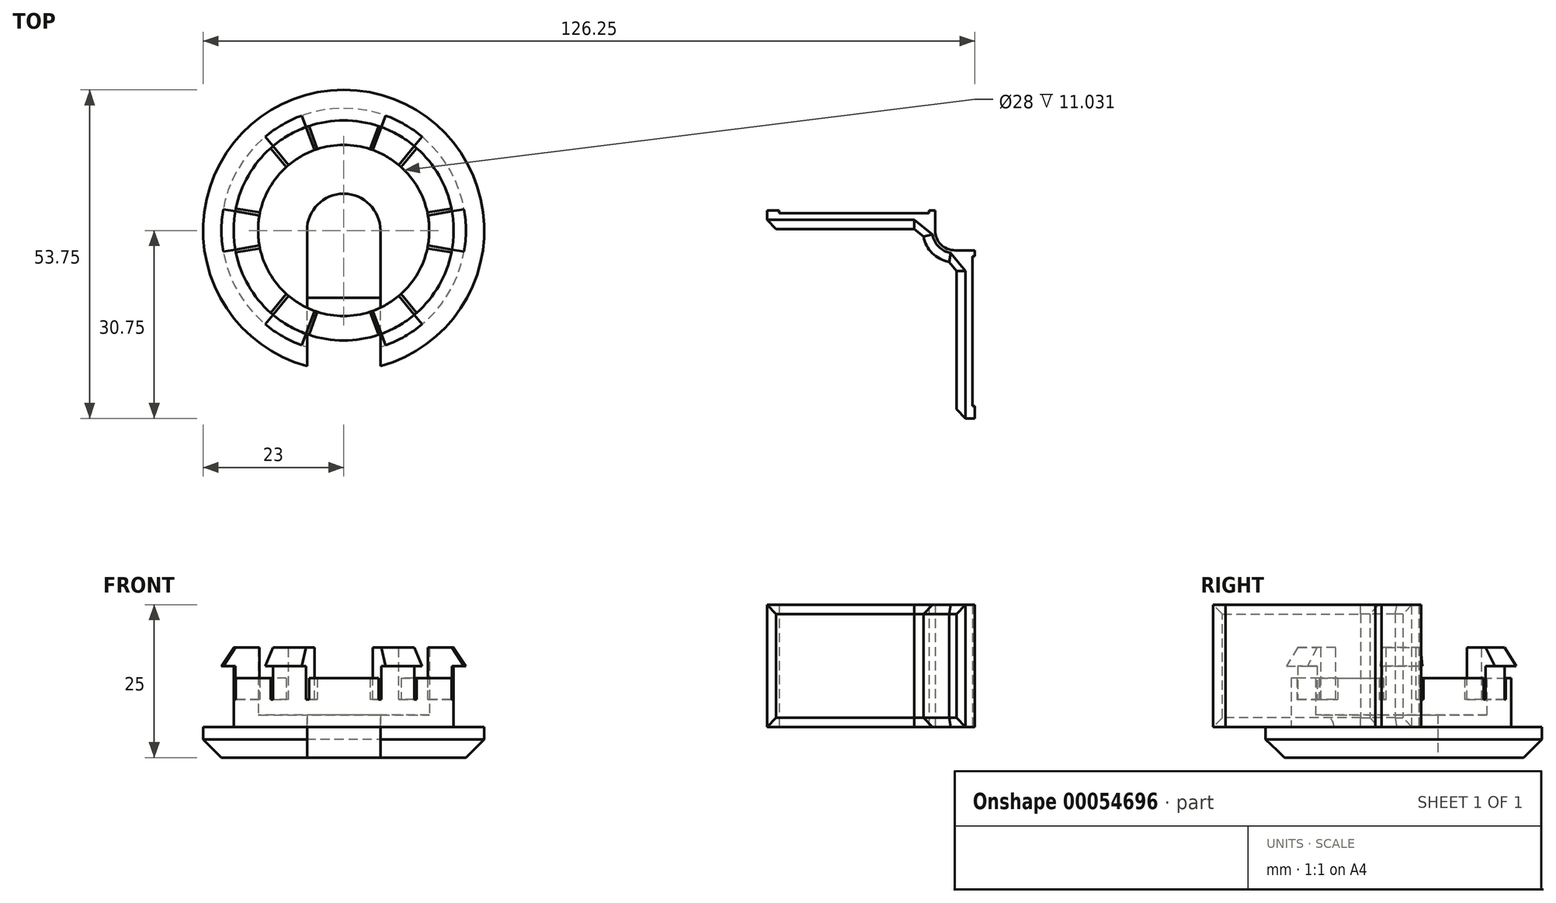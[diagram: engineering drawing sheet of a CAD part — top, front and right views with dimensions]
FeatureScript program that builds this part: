
annotation { "Feature Type Name" : "Feature", "Feature Type Description" : "" }
export const myFeature = defineFeature(function(context is Context, id is Id, definition is map)
    precondition{}
    {
        {
            var Q0;
            Q0=qCreatedBy(makeId("Top.planeOp"),FACE);
            var sketch = newSketch(context, id + "F0", { "sketchPlane" : qUnion([Q0])});
            skCircle(sketch, "E0", {"center": v(0, 0) * mm, "radius": 18 * mm});
            skCircle(sketch, "E1", {"center": v(0, 0) * mm, "radius": 6 * mm});
            skCircle(sketch, "E2", {"center": v(0, 0) * mm, "radius": 23 * mm});
            skCircle(sketch, "E3", {"center": v(0, 0) * mm, "radius": 14 * mm});
            skSolve(sketch);
        }
        {
            var Q0;
            Q0=makeQuery(id+"F0.imprint","IMPRINT",FACE,{"disambiguationData":[TD([[makeQuery(id+"F0.imprint","IMPRINT",EDGE,{"derivedFrom":sQuery(id+"F0.wireOp",EDGE,"E0")}),1.0]])]});
            var Q1;
            Q1=makeQuery(id+"F0.imprint","IMPRINT",FACE,{"disambiguationData":[TD([[makeQuery(id+"F0.imprint","IMPRINT",EDGE,{"derivedFrom":sQuery(id+"F0.wireOp",EDGE,"E1")}),-1.0]])]});
            extrude(context, id + "F1", {"entities" : qUnion([Q0, Q1]), "depth" : 2 * mm});
        }
        {
            var Q0;
            Q0=makeQuery(id+"F0.imprint","IMPRINT",FACE,{"disambiguationData":[TD([[makeQuery(id+"F0.imprint","IMPRINT",EDGE,{"derivedFrom":sQuery(id+"F0.wireOp",EDGE,"E0")}),1.0]])]});
            extrude(context, id + "F2", {"entities" : qUnion([Q0]), "operationType" : NewBodyOperationType.ADD, "depth" : 13 * mm});
        }
        {
            var Q0;
            Q0=makeQuery(id+"F0.imprint","IMPRINT",FACE,{"disambiguationData":[TD([[makeQuery(id+"F0.imprint","IMPRINT",EDGE,{"derivedFrom":sQuery(id+"F0.wireOp",EDGE,"E0")}),-1.0]])]});
            var Q1;
            Q1=makeQuery(id+"F0.imprint","IMPRINT",FACE,{"disambiguationData":[TD([[makeQuery(id+"F0.imprint","IMPRINT",EDGE,{"derivedFrom":sQuery(id+"F0.wireOp",EDGE,"E0")}),1.0]])]});
            var Q2;
            Q2=makeQuery(id+"F0.imprint","IMPRINT",FACE,{"disambiguationData":[TD([[makeQuery(id+"F0.imprint","IMPRINT",EDGE,{"derivedFrom":sQuery(id+"F0.wireOp",EDGE,"E1")}),-1.0]])]});
            extrude(context, id + "F3", {"entities" : qUnion([Q0, Q1, Q2]), "operationType" : NewBodyOperationType.ADD, "oppositeDirection" : true, "depth" : 5 * mm});
        }
        {
            var Q0;
            Q0=makeQuery(id+"F3.opExtrude","CAP_EDGE",EDGE,{"disambiguationData":[OSD([sQuery(id+"F0.wireOp",EDGE,"E2")])],"isStart":false});
            chamfer(context, id + "F4", {"entities" : qUnion([Q0]), "width" : 3 * mm, "tangentPropagation" : true});
        }
        {
            var Q0;
            Q0=qCreatedBy(makeId("Right.planeOp"),FACE);
            var sketch = newSketch(context, id + "F5", { "sketchPlane" : qUnion([Q0])});
            skLineSegment(sketch, "E4", {"start": v(0, 30.83) * mm, "end": v(0, -5) * mm});
            skLineSegment(sketch, "E5", {"start": v(0, -5) * mm, "end": v(-46.75, -5) * mm});
            skLineSegment(sketch, "E6", {"start": v(-46.75, -5) * mm, "end": v(-46.75, 0) * mm});
            skLineSegment(sketch, "E7", {"start": v(-46.75, 0) * mm, "end": v(-11, 0) * mm});
            skLineSegment(sketch, "E8", {"start": v(-11, 0) * mm, "end": v(-6, 5) * mm});
            skLineSegment(sketch, "E9", {"start": v(-6, 5) * mm, "end": v(-6, 30.83) * mm});
            skLineSegment(sketch, "E10", {"start": v(-6, 30.83) * mm, "end": v(0, 30.83) * mm});
            skSolve(sketch);
        }
        {
            var Q0;
            Q0=makeQuery(id+"F5.imprint","IMPRINT",FACE,{"disambiguationData":[TD([[makeQuery(id+"F5.imprint","IMPRINT",EDGE,{"derivedFrom":sQuery(id+"F5.wireOp",EDGE,"E4")}),-1.0]])]});
            extrude(context, id + "F6", {"entities" : qUnion([Q0]), "operationType" : NewBodyOperationType.REMOVE, "endBound" : BoundingType.SYMMETRIC, "oppositeDirection" : true, "depth" : 12 * mm});
        }
        {
            var Q0;
            Q0=makeQuery(id+"F6.boolean.opBoolean","INTERSECT",EDGE,{"derivedFrom":[makeQuery(id+"F1.opExtrude","CAP_FACE",FACE,{"disambiguationData":[OSD([sQuery(id+"F0.wireOp",EDGE,"E0"),sQuery(id+"F0.wireOp",EDGE,"E1")])],"isStart":false}),makeQuery(id+"F6.opExtrude","SWEPT_FACE",FACE,{"disambiguationData":[OSD([sQuery(id+"F5.wireOp",EDGE,"E8")])]})]});
            fillet(context, id + "F7", {"entities" : qUnion([Q0]), "radius" : 2 * mm, "tangentPropagation" : true, "allowEdgeOverflow" : false});
        }
        {
            var Q0;
            Q0=qCreatedBy(makeId("Front.planeOp"),FACE);
            var sketch = newSketch(context, id + "F8", { "sketchPlane" : qUnion([Q0])});
            skLineSegment(sketch, "E11", {"start": v(14, 10) * mm, "end": v(14, 13) * mm});
            skLineSegment(sketch, "E12", {"start": v(14, 13) * mm, "end": v(18, 13) * mm});
            skLineSegment(sketch, "E13", {"start": v(18, 13) * mm, "end": v(20, 10) * mm});
            skLineSegment(sketch, "E14", {"start": v(20, 10) * mm, "end": v(14, 10) * mm});
            skLineSegment(sketch, "E15", {"start": v(0, 0) * mm, "end": v(0, 19.84) * mm});
            skLineSegment(sketch, "E16", {"start": v(18, 13) * mm, "end": v(18, 5) * mm});
            skLineSegment(sketch, "E17", {"start": v(18, 5) * mm, "end": v(14, 5) * mm});
            skLineSegment(sketch, "E18", {"start": v(14, 5) * mm, "end": v(14, 10) * mm});
            skSolve(sketch);
        }
        {
            var Q0;
            Q0=makeQuery(id+"F8.imprint","IMPRINT",FACE,{"disambiguationData":[TD([[makeQuery(id+"F8.imprint","IMPRINT",EDGE,{"derivedFrom":sQuery(id+"F8.wireOp",EDGE,"E11")}),-1.0]])]});
            var Q1;
            {var subQ0=sQuery(id+"F8.wireOp",EDGE,"E13");Q1=makeQuery(id+"F8.imprint","IMPRINT",FACE,{"disambiguationData":[TD([[makeQuery(id+"F8.imprint","IMPRINT",EDGE,{"derivedFrom":subQ0}),-1.0]])]});}
            var Q2;
            {var subQ4=sQuery(id+"F8.wireOp",EDGE,"E17");Q2=makeQuery(id+"F8.imprint","IMPRINT",FACE,{"disambiguationData":[TD([[makeQuery(id+"F8.imprint","IMPRINT",EDGE,{"derivedFrom":subQ4}),-1.0]])]});}
            var Q3;
            Q3=sQuery(id+"F8.wireOp",EDGE,"E15");
            revolve(context, id + "F9", {"entities" : qUnion([Q0, Q1, Q2]), "axis" : qUnion([Q3]), "revolveType" : RevolveType.SYMMETRIC, "angle" : 20 * degree});
        }
        {
            var Q0;
            Q0=makeQuery(id+"F9.opRevolve","SWEPT_BODY",BODY,{"disambiguationData":[OSD([sQuery(id+"F8.wireOp",EDGE,"E11"),sQuery(id+"F8.wireOp",EDGE,"E12"),sQuery(id+"F8.wireOp",EDGE,"E13"),sQuery(id+"F8.wireOp",EDGE,"E14")])]});
            var Q1;
            Q1=sQuery(id+"F8.wireOp",EDGE,"E15");
            circularPattern(context, id + "F10", {"entities" : qUnion([Q0]), "axis" : qUnion([Q1]), "angle" : 360 * degree, "instanceCount" : 6, "equalSpace" : true});
        }
        {
            var Q0;
            Q0=makeQuery(id+"F9.opRevolve","SWEPT_BODY",BODY,{"disambiguationData":[OSD([sQuery(id+"F8.wireOp",EDGE,"E11"),sQuery(id+"F8.wireOp",EDGE,"E12"),sQuery(id+"F8.wireOp",EDGE,"E13"),sQuery(id+"F8.wireOp",EDGE,"E14"),sQuery(id+"F8.wireOp",EDGE,"E16"),sQuery(id+"F8.wireOp",EDGE,"E17"),sQuery(id+"F8.wireOp",EDGE,"E18")])]});
            var Q1;
            Q1=makeQuery(id+"F10.opPattern","COPY",BODY,{"derivedFrom":makeQuery(id+"F9.opRevolve","SWEPT_BODY",BODY,{"disambiguationData":[OSD([sQuery(id+"F8.wireOp",EDGE,"E11"),sQuery(id+"F8.wireOp",EDGE,"E12"),sQuery(id+"F8.wireOp",EDGE,"E13"),sQuery(id+"F8.wireOp",EDGE,"E14"),sQuery(id+"F8.wireOp",EDGE,"E16"),sQuery(id+"F8.wireOp",EDGE,"E17"),sQuery(id+"F8.wireOp",EDGE,"E18")])]}),"instanceName":"1"});
            var Q2;
            Q2=makeQuery(id+"F10.opPattern","COPY",BODY,{"derivedFrom":makeQuery(id+"F9.opRevolve","SWEPT_BODY",BODY,{"disambiguationData":[OSD([sQuery(id+"F8.wireOp",EDGE,"E11"),sQuery(id+"F8.wireOp",EDGE,"E12"),sQuery(id+"F8.wireOp",EDGE,"E13"),sQuery(id+"F8.wireOp",EDGE,"E14"),sQuery(id+"F8.wireOp",EDGE,"E16"),sQuery(id+"F8.wireOp",EDGE,"E17"),sQuery(id+"F8.wireOp",EDGE,"E18")])]}),"instanceName":"2"});
            var Q3;
            Q3=makeQuery(id+"F10.opPattern","COPY",BODY,{"derivedFrom":makeQuery(id+"F9.opRevolve","SWEPT_BODY",BODY,{"disambiguationData":[OSD([sQuery(id+"F8.wireOp",EDGE,"E11"),sQuery(id+"F8.wireOp",EDGE,"E12"),sQuery(id+"F8.wireOp",EDGE,"E13"),sQuery(id+"F8.wireOp",EDGE,"E14"),sQuery(id+"F8.wireOp",EDGE,"E16"),sQuery(id+"F8.wireOp",EDGE,"E17"),sQuery(id+"F8.wireOp",EDGE,"E18")])]}),"instanceName":"3"});
            var Q4;
            Q4=makeQuery(id+"F10.opPattern","COPY",BODY,{"derivedFrom":makeQuery(id+"F9.opRevolve","SWEPT_BODY",BODY,{"disambiguationData":[OSD([sQuery(id+"F8.wireOp",EDGE,"E11"),sQuery(id+"F8.wireOp",EDGE,"E12"),sQuery(id+"F8.wireOp",EDGE,"E13"),sQuery(id+"F8.wireOp",EDGE,"E14"),sQuery(id+"F8.wireOp",EDGE,"E16"),sQuery(id+"F8.wireOp",EDGE,"E17"),sQuery(id+"F8.wireOp",EDGE,"E18")])]}),"instanceName":"4"});
            var Q5;
            Q5=makeQuery(id+"F10.opPattern","COPY",BODY,{"derivedFrom":makeQuery(id+"F9.opRevolve","SWEPT_BODY",BODY,{"disambiguationData":[OSD([sQuery(id+"F8.wireOp",EDGE,"E11"),sQuery(id+"F8.wireOp",EDGE,"E12"),sQuery(id+"F8.wireOp",EDGE,"E13"),sQuery(id+"F8.wireOp",EDGE,"E14"),sQuery(id+"F8.wireOp",EDGE,"E16"),sQuery(id+"F8.wireOp",EDGE,"E17"),sQuery(id+"F8.wireOp",EDGE,"E18")])]}),"instanceName":"5"});
            var Q6;
            Q6=makeQuery(id+"F1.opExtrude","SWEPT_BODY",BODY,{"disambiguationData":[OSD([sQuery(id+"F0.wireOp",EDGE,"E0"),sQuery(id+"F0.wireOp",EDGE,"E1")])]});
            booleanBodies(context, id + "F11", {"operationType" : BooleanOperationType.SUBTRACTION, "tools" : qUnion([Q0, Q1, Q2, Q3, Q4, Q5]), "targets" : qUnion([Q6]), "offset" : true, "offsetAll" : true, "offsetDistance" : 0.5 * mm, "keepTools" : true});
        }
        {
            var Q0;
            Q0=makeQuery(id+"F10.opPattern","COPY",FACE,{"derivedFrom":makeQuery(id+"F9.opRevolve","SWEPT_FACE",FACE,{"disambiguationData":[OSD([sQuery(id+"F8.wireOp",EDGE,"E17")])]}),"instanceName":"4"});
            var Q1;
            Q1=makeQuery(id+"F10.opPattern","COPY",FACE,{"derivedFrom":makeQuery(id+"F9.opRevolve","SWEPT_FACE",FACE,{"disambiguationData":[OSD([sQuery(id+"F8.wireOp",EDGE,"E17")])]}),"instanceName":"5"});
            var Q2;
            Q2=makeQuery(id+"F9.opRevolve","SWEPT_FACE",FACE,{"disambiguationData":[OSD([sQuery(id+"F8.wireOp",EDGE,"E17")])]});
            var Q3;
            Q3=makeQuery(id+"F10.opPattern","COPY",FACE,{"derivedFrom":makeQuery(id+"F9.opRevolve","SWEPT_FACE",FACE,{"disambiguationData":[OSD([sQuery(id+"F8.wireOp",EDGE,"E17")])]}),"instanceName":"1"});
            var Q4;
            Q4=makeQuery(id+"F10.opPattern","COPY",FACE,{"derivedFrom":makeQuery(id+"F9.opRevolve","SWEPT_FACE",FACE,{"disambiguationData":[OSD([sQuery(id+"F8.wireOp",EDGE,"E17")])]}),"instanceName":"2"});
            var Q5;
            Q5=makeQuery(id+"F10.opPattern","COPY",FACE,{"derivedFrom":makeQuery(id+"F9.opRevolve","SWEPT_FACE",FACE,{"disambiguationData":[OSD([sQuery(id+"F8.wireOp",EDGE,"E17")])]}),"instanceName":"3"});
            extrude(context, id + "F12", {"entities" : qUnion([Q0, Q1, Q2, Q3, Q4, Q5]), "operationType" : NewBodyOperationType.ADD, "depth" : 5 * mm});
        }
        {
            var Q0;
            {var subQ0=sQuery(id+"F8.wireOp",EDGE,"E18");var subQ1=sQuery(id+"F8.wireOp",EDGE,"E17");var subQ2=sQuery(id+"F8.wireOp",EDGE,"E16");var subQ3=sQuery(id+"F8.wireOp",EDGE,"E14");var subQ4=sQuery(id+"F8.wireOp",EDGE,"E13");var subQ5=sQuery(id+"F8.wireOp",EDGE,"E12");var subQ6=sQuery(id+"F8.wireOp",EDGE,"E11");var subQ7=sQuery(id+"F0.wireOp",EDGE,"E0");var subQ8=sQuery(id+"F0.wireOp",EDGE,"E3");Q0=makeQuery(id+"F11.tempBoolean.opBoolean","SPLIT",FACE,{"disambiguationData":[TD([makeQuery(id+"F11.offsetTempBody.opPattern","COPY",FACE,{"derivedFrom":makeQuery(id+"F10.opPattern","COPY",FACE,{"derivedFrom":makeQuery(id+"F9.opRevolve","CAP_FACE",FACE,{"disambiguationData":[OSD([subQ6,subQ5,subQ4,subQ3,subQ2,subQ1,subQ0])],"isStart":false}),"instanceName":"2"}),"instanceName":"1"})])],"derivedFrom":makeQuery(id+"F2.opExtrude","CAP_FACE",FACE,{"disambiguationData":[OSD([subQ7,subQ8])],"isStart":false})});}
            var Q1;
            {var subQ0=sQuery(id+"F0.wireOp",EDGE,"E3");var subQ1=sQuery(id+"F0.wireOp",EDGE,"E0");var subQ2=sQuery(id+"F8.wireOp",EDGE,"E18");var subQ3=sQuery(id+"F8.wireOp",EDGE,"E17");var subQ4=sQuery(id+"F8.wireOp",EDGE,"E16");var subQ5=sQuery(id+"F8.wireOp",EDGE,"E14");var subQ6=sQuery(id+"F8.wireOp",EDGE,"E13");var subQ7=sQuery(id+"F8.wireOp",EDGE,"E12");var subQ8=sQuery(id+"F8.wireOp",EDGE,"E11");Q1=makeQuery(id+"F11.tempBoolean.opBoolean","SPLIT",FACE,{"disambiguationData":[TD([makeQuery(id+"F11.offsetTempBody.opPattern","COPY",FACE,{"derivedFrom":makeQuery(id+"F10.opPattern","COPY",FACE,{"derivedFrom":makeQuery(id+"F9.opRevolve","CAP_FACE",FACE,{"disambiguationData":[OSD([subQ8,subQ7,subQ6,subQ5,subQ4,subQ3,subQ2])],"isStart":false}),"instanceName":"3"}),"instanceName":"1"})])],"derivedFrom":makeQuery(id+"F2.opExtrude","CAP_FACE",FACE,{"disambiguationData":[OSD([subQ1,subQ0])],"isStart":false})});}
            var Q2;
            {var subQ0=sQuery(id+"F8.wireOp",EDGE,"E18");var subQ1=sQuery(id+"F8.wireOp",EDGE,"E17");var subQ2=sQuery(id+"F8.wireOp",EDGE,"E16");var subQ3=sQuery(id+"F8.wireOp",EDGE,"E14");var subQ4=sQuery(id+"F8.wireOp",EDGE,"E13");var subQ5=sQuery(id+"F8.wireOp",EDGE,"E12");var subQ6=sQuery(id+"F8.wireOp",EDGE,"E11");var subQ7=sQuery(id+"F0.wireOp",EDGE,"E3");var subQ8=sQuery(id+"F0.wireOp",EDGE,"E0");Q2=makeQuery(id+"F11.tempBoolean.opBoolean","SPLIT",FACE,{"disambiguationData":[TD([makeQuery(id+"F11.offsetTempBody.opPattern","COPY",FACE,{"derivedFrom":makeQuery(id+"F10.opPattern","COPY",FACE,{"derivedFrom":makeQuery(id+"F9.opRevolve","CAP_FACE",FACE,{"disambiguationData":[OSD([subQ6,subQ5,subQ4,subQ3,subQ2,subQ1,subQ0])],"isStart":false}),"instanceName":"4"}),"instanceName":"1"})])],"derivedFrom":makeQuery(id+"F2.opExtrude","CAP_FACE",FACE,{"disambiguationData":[OSD([subQ8,subQ7])],"isStart":false})});}
            var Q3;
            {var subQ0=sQuery(id+"F0.wireOp",EDGE,"E3");var subQ1=sQuery(id+"F0.wireOp",EDGE,"E0");var subQ2=sQuery(id+"F8.wireOp",EDGE,"E18");var subQ3=sQuery(id+"F8.wireOp",EDGE,"E17");var subQ4=sQuery(id+"F8.wireOp",EDGE,"E16");var subQ5=sQuery(id+"F8.wireOp",EDGE,"E14");var subQ6=sQuery(id+"F8.wireOp",EDGE,"E13");var subQ7=sQuery(id+"F8.wireOp",EDGE,"E12");var subQ8=sQuery(id+"F8.wireOp",EDGE,"E11");Q3=makeQuery(id+"F11.tempBoolean.opBoolean","SPLIT",FACE,{"disambiguationData":[TD([makeQuery(id+"F11.offsetTempBody.opPattern","COPY",FACE,{"derivedFrom":makeQuery(id+"F9.opRevolve","CAP_FACE",FACE,{"disambiguationData":[OSD([subQ8,subQ7,subQ6,subQ5,subQ4,subQ3,subQ2])],"isStart":true}),"instanceName":"1"})])],"derivedFrom":makeQuery(id+"F2.opExtrude","CAP_FACE",FACE,{"disambiguationData":[OSD([subQ1,subQ0])],"isStart":false})});}
            var Q4;
            {var subQ0=sQuery(id+"F0.wireOp",EDGE,"E3");var subQ1=sQuery(id+"F8.wireOp",EDGE,"E18");var subQ2=sQuery(id+"F8.wireOp",EDGE,"E17");var subQ3=sQuery(id+"F8.wireOp",EDGE,"E16");var subQ4=sQuery(id+"F8.wireOp",EDGE,"E14");var subQ5=sQuery(id+"F8.wireOp",EDGE,"E13");var subQ6=sQuery(id+"F8.wireOp",EDGE,"E12");var subQ7=sQuery(id+"F8.wireOp",EDGE,"E11");var subQ8=sQuery(id+"F0.wireOp",EDGE,"E0");Q4=makeQuery(id+"F11.tempBoolean.opBoolean","SPLIT",FACE,{"disambiguationData":[TD([makeQuery(id+"F11.offsetTempBody.opPattern","COPY",FACE,{"derivedFrom":makeQuery(id+"F9.opRevolve","CAP_FACE",FACE,{"disambiguationData":[OSD([subQ7,subQ6,subQ5,subQ4,subQ3,subQ2,subQ1])],"isStart":false}),"instanceName":"1"})])],"derivedFrom":makeQuery(id+"F2.opExtrude","CAP_FACE",FACE,{"disambiguationData":[OSD([subQ8,subQ0])],"isStart":false})});}
            var Q5;
            {var subQ0=sQuery(id+"F8.wireOp",EDGE,"E18");var subQ1=sQuery(id+"F8.wireOp",EDGE,"E17");var subQ2=sQuery(id+"F8.wireOp",EDGE,"E16");var subQ3=sQuery(id+"F8.wireOp",EDGE,"E14");var subQ4=sQuery(id+"F8.wireOp",EDGE,"E13");var subQ5=sQuery(id+"F8.wireOp",EDGE,"E12");var subQ6=sQuery(id+"F8.wireOp",EDGE,"E11");var subQ7=sQuery(id+"F0.wireOp",EDGE,"E3");var subQ8=sQuery(id+"F0.wireOp",EDGE,"E0");Q5=makeQuery(id+"F11.tempBoolean.opBoolean","SPLIT",FACE,{"disambiguationData":[TD([makeQuery(id+"F11.offsetTempBody.opPattern","COPY",FACE,{"derivedFrom":makeQuery(id+"F10.opPattern","COPY",FACE,{"derivedFrom":makeQuery(id+"F9.opRevolve","CAP_FACE",FACE,{"disambiguationData":[OSD([subQ6,subQ5,subQ4,subQ3,subQ2,subQ1,subQ0])],"isStart":false}),"instanceName":"1"}),"instanceName":"1"})])],"derivedFrom":makeQuery(id+"F2.opExtrude","CAP_FACE",FACE,{"disambiguationData":[OSD([subQ8,subQ7])],"isStart":false})});}
            extrude(context, id + "F13", {"entities" : qUnion([Q0, Q1, Q2, Q3, Q4, Q5]), "operationType" : NewBodyOperationType.REMOVE, "oppositeDirection" : true, "depth" : 5 * mm});
        }
        {
            var Q0;
            Q0=qCreatedBy(makeId("Top.planeOp"),FACE);
            var sketch = newSketch(context, id + "F14", { "sketchPlane" : qUnion([Q0])});
            skLineSegment(sketch, "E19", {"start": v(69.25, 3.25) * mm, "end": v(103.25, 3.25) * mm});
            skLineSegment(sketch, "E20", {"start": v(103.25, 3.25) * mm, "end": v(103.25, -30.75) * mm});
            skLineSegment(sketch, "E21", {"start": v(103.25, -30.75) * mm, "end": v(100.25, -30.75) * mm});
            skLineSegment(sketch, "E22", {"start": v(100.25, -30.75) * mm, "end": v(100.25, 0.25) * mm});
            skLineSegment(sketch, "E23", {"start": v(100.25, 0.25) * mm, "end": v(69.25, 0.25) * mm});
            skLineSegment(sketch, "E24", {"start": v(69.25, 0.25) * mm, "end": v(69.25, 3.25) * mm});
            skCircle(sketch, "E25", {"center": v(100, 0) * mm, "radius": 3.25 * mm});
            skArc(sketch, "E26", {"start": v(94.76, 0.25) * mm, "mid": v(96.29, -3.71) * mm, "end": v(100.25, -5.24) * mm});
            skLineSegment(sketch, "E27", {"start": v(103.25, -4.25) * mm, "end": v(102.85, -4.25) * mm});
            skLineSegment(sketch, "E28", {"start": v(102.85, -4.25) * mm, "end": v(102.85, -28.75) * mm});
            skLineSegment(sketch, "E29", {"start": v(102.85, -28.75) * mm, "end": v(103.25, -28.75) * mm});
            skLineSegment(sketch, "E30", {"start": v(103.25, 3.25) * mm, "end": v(74.75, -25.25) * mm});
            skLineSegment(sketch, "E31.MirrorCS", {"start": v(95.75, 3.25) * mm, "end": v(95.75, 2.85) * mm});
            skLineSegment(sketch, "E32.MirrorCS", {"start": v(95.75, 2.85) * mm, "end": v(71.25, 2.85) * mm});
            skLineSegment(sketch, "E33.MirrorCS", {"start": v(71.25, 2.85) * mm, "end": v(71.25, 3.25) * mm});
            skLineSegment(sketch, "E34", {"start": v(100, -3.25) * mm, "end": v(103.25, -3.25) * mm});
            skLineSegment(sketch, "E35", {"start": v(96.75, 0) * mm, "end": v(96.75, 3.25) * mm});
            skSolve(sketch);
        }
        {
            var Q0;
            {var subQ0=sQuery(id+"F14.wireOp",EDGE,"E24");Q0=makeQuery(id+"F14.imprint","IMPRINT",FACE,{"disambiguationData":[TD([[makeQuery(id+"F14.imprint","IMPRINT",EDGE,{"derivedFrom":subQ0}),-1.0]])]});}
            var Q1;
            {var subQ1=sQuery(id+"F14.wireOp",EDGE,"E26");var subQ5=sQuery(id+"F14.wireOp",EDGE,"E23");var subQ6=makeQuery(id+"F14.imprint","INTERSECT",VERTEX,{"derivedFrom":[subQ5,subQ1]});Q1=makeQuery(id+"F14.imprint","IMPRINT",FACE,{"disambiguationData":[TD([[makeQuery(id+"F14.imprint","IMPRINT",EDGE,{"disambiguationData":[TD([[subQ6,1.0]])],"derivedFrom":subQ5}),1.0]])]});}
            var Q2;
            {var subQ1=sQuery(id+"F14.wireOp",EDGE,"E26");var subQ7=sQuery(id+"F14.wireOp",EDGE,"E22");var subQ8=makeQuery(id+"F14.imprint","INTERSECT",VERTEX,{"derivedFrom":[subQ7,subQ1]});Q2=makeQuery(id+"F14.imprint","IMPRINT",FACE,{"disambiguationData":[TD([[makeQuery(id+"F14.imprint","IMPRINT",EDGE,{"disambiguationData":[TD([[subQ8,-1.0]])],"derivedFrom":subQ7}),1.0]])]});}
            var Q3;
            {var subQ1=sQuery(id+"F14.wireOp",EDGE,"E21");Q3=makeQuery(id+"F14.imprint","IMPRINT",FACE,{"disambiguationData":[TD([[makeQuery(id+"F14.imprint","IMPRINT",EDGE,{"derivedFrom":subQ1}),-1.0]])]});}
            extrude(context, id + "F15", {"entities" : qUnion([Q0, Q1, Q2, Q3]), "depth" : 20 * mm});
        }
        {
            var Q0;
            Q0=makeQuery(id+"F15.opExtrude","SWEPT_FACE",FACE,{"disambiguationData":[OSD([sQuery(id+"F14.wireOp",EDGE,"E23")])]});
            var Q1;
            Q1=makeQuery(id+"F15.opExtrude","SWEPT_FACE",FACE,{"disambiguationData":[OSD([sQuery(id+"F14.wireOp",EDGE,"E22")])]});
            chamfer(context, id + "F16", {"entities" : qUnion([Q0, Q1]), "width" : 1.5 * mm, "tangentPropagation" : true});
        }
    });
